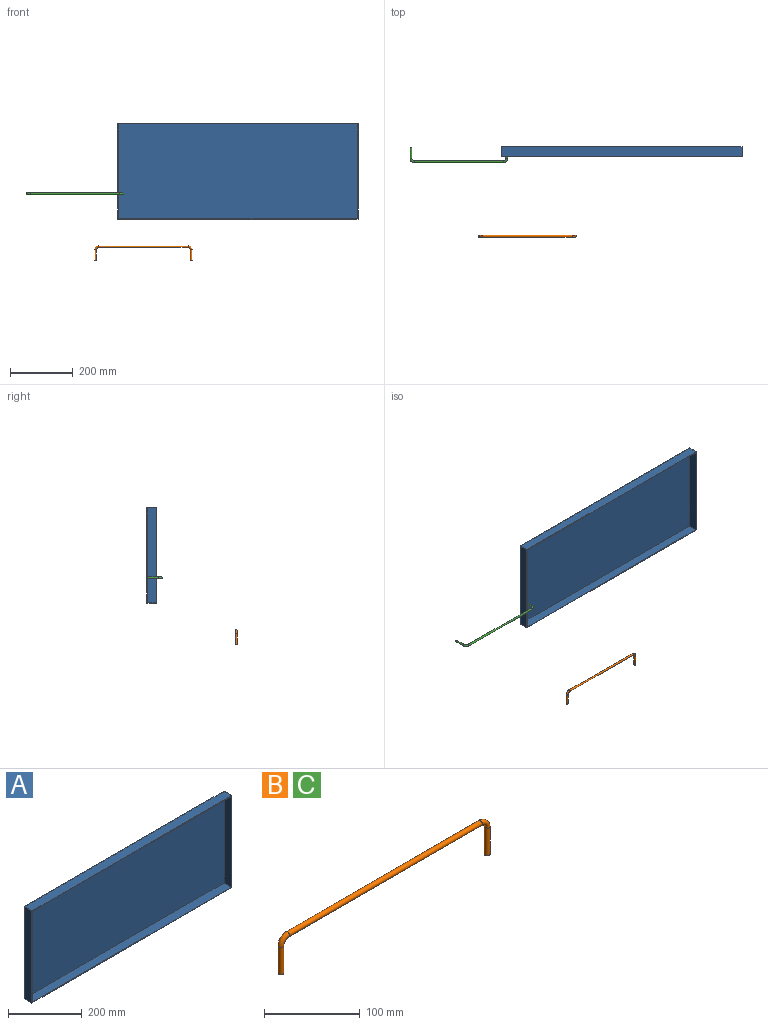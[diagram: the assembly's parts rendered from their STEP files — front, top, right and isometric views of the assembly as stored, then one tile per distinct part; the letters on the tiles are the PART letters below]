
ASSEMBLY  parts=3 mates=1
PART A: 11 faces, bbox 765x30x305 mm
  f0: plane 765x305mm, normal (0,-1,0), area 4264mm2, adj f1,f2,f3,f4,f6,f7,f8,f9
  f1: plane 305x30mm, normal (-1,0,0), area 9150mm2, adj f0,f2,f4,f5
  f2: plane 765x30mm, normal (0,0,-1), area 22950mm2, adj f0,f1,f3,f5
  f3: plane 305x30mm, normal (1,0,0), area 9150mm2, adj f0,f2,f4,f5
  f4: plane 765x30mm, normal (0,0,1), area 22950mm2, adj f0,f1,f3,f5
  f5: plane 765x305mm, normal (0,1,0), area 233325mm2, adj f1,f2,f3,f4
  f6: plane 301x28mm, normal (1,0,0), area 8428mm2, adj f0,f7,f9,f10
  f7: plane 761x28mm, normal (0,0,1), area 21308mm2, adj f0,f6,f8,f10
  f8: plane 301x28mm, normal (-1,0,0), area 8428mm2, adj f0,f7,f9,f10
  f9: plane 761x28mm, normal (0,0,-1), area 21308mm2, adj f0,f6,f8,f10
  f10: plane 761x301mm, normal (0,-1,0), area 229061mm2, adj f6,f7,f8,f9
PART B: 7 faces, bbox 313.1x6x49.1 mm
  f0: plane 6x6mm, normal (0,0,-1), area 28.3mm2, adj f2
  f1: plane 6x6mm, normal (0,0,-1), area 28.3mm2, adj f6
  f2: cylinder r=3mm len=35mm, axis (0,0,1), area 659.7mm2, adj f0,f3
  f3: torus R=10mm, axis (0,1,0), area 296.1mm2, adj f2,f4
  f4: cylinder r=3mm len=285mm, axis (1,0,0), area 5372.1mm2, adj f3,f5
  f5: torus R=10mm, axis (0,1,0), area 296.1mm2, adj f4,f6
  f6: cylinder r=3mm len=35mm, axis (0,0,-1), area 659.7mm2, adj f1,f5
PART C: same geometry as B
PLACE A t=(32.72,164.33,127.25)mm
PLACE B t=(-38.82,-119.78,-5.24)mm
PLACE C rot(axis=(1,0,0),90deg) t=(-257.1,162.33,207.5)mm
MATE planar C.f6 <-> A.f10  axis (0,1,0) through (47.9,162.33,207.5)mm
